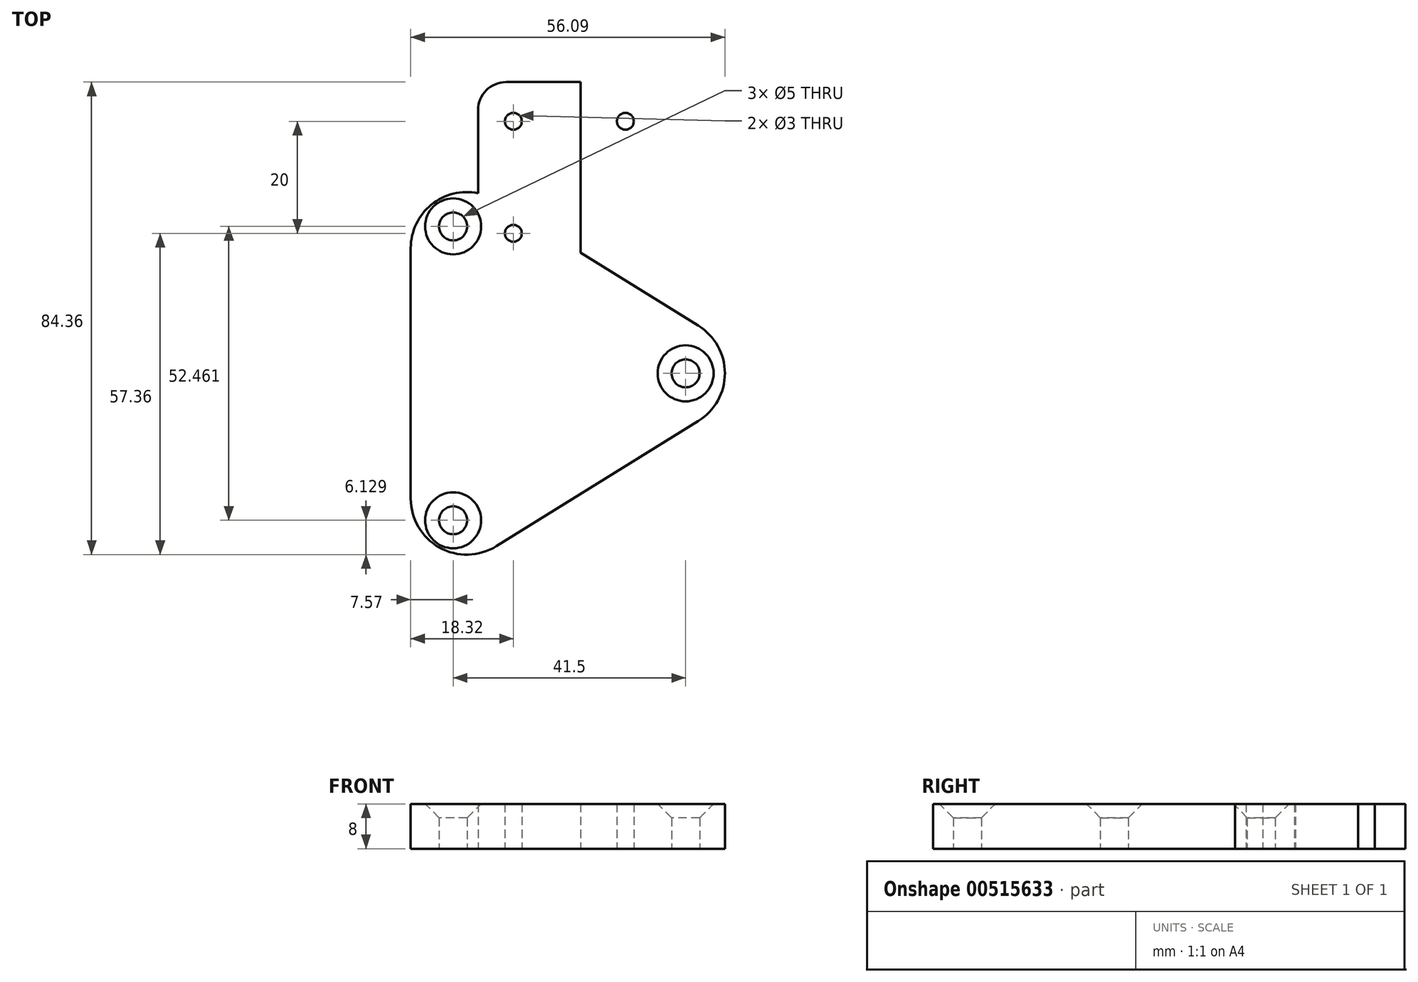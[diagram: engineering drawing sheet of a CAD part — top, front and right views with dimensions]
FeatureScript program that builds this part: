
annotation { "Feature Type Name" : "Feature", "Feature Type Description" : "" }
export const myFeature = defineFeature(function(context is Context, id is Id, definition is map)
    precondition{}
    {
        {
            var Q0;
            Q0=qCreatedBy(makeId("Top.planeOp"),FACE);
            var sketch = newSketch(context, id + "F0", { "sketchPlane" : qUnion([Q0])});
            skCircle(sketch, "E0", {"center": v(-22.75, 26.23) * mm, "radius": 2.5 * mm});
            skCircle(sketch, "E1.MirrorC", {"center": v(-22.75, -26.23) * mm, "radius": 2.5 * mm});
            skCircle(sketch, "E2", {"center": v(18.75, 0) * mm, "radius": 2.5 * mm});
            skCircle(sketch, "E3", {"center": v(-12, 45) * mm, "radius": 1.5 * mm});
            skCircle(sketch, "E4.MirrorC", {"center": v(8, 45) * mm, "radius": 1.5 * mm});
            skCircle(sketch, "E5.MirrorC", {"center": v(8, 25) * mm, "radius": 1.5 * mm});
            skLineSegment(sketch, "E6", {"start": v(21.03, -8.5) * mm, "end": v(-15.05, -30.86) * mm});
            skLineSegment(sketch, "E7", {"start": v(21.03, 8.5) * mm, "end": v(-15.05, 30.86) * mm});
            skPoint(sketch, "E8", {"position": v(34.75, 0) * mm});
            skLineSegment(sketch, "E9", {"start": v(-30.32, -22.36) * mm, "end": v(-30.32, 22.36) * mm});
            skPoint(sketch, "E10.visualSharp", {"position": v(-30.32, 40.33) * mm});
            skArc(sketch, "E10.filletArc", {"start": v(-15.05, 30.86) * mm, "mid": v(-25.18, 31.1) * mm, "end": v(-30.32, 22.36) * mm});
            skPoint(sketch, "E11.visualSharp", {"position": v(-30.32, -40.33) * mm});
            skArc(sketch, "E11.filletArc", {"start": v(-30.32, -22.36) * mm, "mid": v(-25.18, -31.1) * mm, "end": v(-15.05, -30.86) * mm});
            skArc(sketch, "E12.filletArc", {"start": v(21.03, -8.5) * mm, "mid": v(25.77, 0) * mm, "end": v(21.03, 8.5) * mm});
            skCircle(sketch, "E13", {"center": v(-12, 25) * mm, "radius": 1.5 * mm});
            skLineSegment(sketch, "E14.top", {"start": v(-13.3, 52) * mm, "end": v(9.3, 52) * mm});
            skLineSegment(sketch, "E14.left", {"start": v(-18.3, 32.16) * mm, "end": v(-18.3, 47) * mm});
            skLineSegment(sketch, "E14.right", {"start": v(14.3, 12.67) * mm, "end": v(14.3, 47) * mm});
            skPoint(sketch, "E15.visualSharp", {"position": v(-18.3, 52) * mm});
            skArc(sketch, "E15.filletArc", {"start": v(-13.3, 52) * mm, "mid": v(-16.84, 50.53) * mm, "end": v(-18.3, 47) * mm});
            skPoint(sketch, "E16.visualSharp", {"position": v(14.3, 52) * mm});
            skArc(sketch, "E16.filletArc", {"start": v(14.3, 47) * mm, "mid": v(12.84, 50.53) * mm, "end": v(9.3, 52) * mm});
            skLineSegment(sketch, "E17", {"start": v(-4, 52) * mm, "end": v(-4, -24.02) * mm});
            skLineSegment(sketch, "E18", {"start": v(0, 52) * mm, "end": v(0, -21.54) * mm});
            skSolve(sketch);
        }
        {
            var Q0;
            Q0=makeQuery(id+"F0.imprint","IMPRINT",FACE,{"disambiguationData":[TD([[makeQuery(id+"F0.imprint","IMPRINT",EDGE,{"derivedFrom":sQuery(id+"F0.wireOp",EDGE,"E0")}),-1.0]])]});
            var Q1;
            {var subQ0=sQuery(id+"F0.wireOp",EDGE,"E17");var subQ1=sQuery(id+"F0.wireOp",EDGE,"E6");var subQ2=makeQuery(id+"F0.imprint","INTERSECT",VERTEX,{"derivedFrom":[subQ1,subQ0]});Q1=makeQuery(id+"F0.imprint","IMPRINT",FACE,{"disambiguationData":[TD([[makeQuery(id+"F0.imprint","IMPRINT",EDGE,{"disambiguationData":[TD([[subQ2,1.0]])],"derivedFrom":subQ1}),-1.0]])]});}
            var Q2;
            Q2=makeQuery(id+"F0.imprint","IMPRINT",FACE,{"disambiguationData":[TD([[makeQuery(id+"F0.imprint","IMPRINT",EDGE,{"derivedFrom":sQuery(id+"F0.wireOp",EDGE,"E2")}),-1.0]])]});
            var Q3;
            Q3=makeQuery(id+"F0.imprint","IMPRINT",FACE,{"disambiguationData":[TD([[makeQuery(id+"F0.imprint","IMPRINT",EDGE,{"derivedFrom":sQuery(id+"F0.wireOp",EDGE,"E4.MirrorC")}),1.0]])]});
            var Q4;
            {var subQ0=sQuery(id+"F0.wireOp",EDGE,"E18");var subQ1=sQuery(id+"F0.wireOp",EDGE,"E7");var subQ2=makeQuery(id+"F0.imprint","INTERSECT",VERTEX,{"derivedFrom":[subQ1,subQ0]});Q4=makeQuery(id+"F0.imprint","IMPRINT",FACE,{"disambiguationData":[TD([[makeQuery(id+"F0.imprint","IMPRINT",EDGE,{"disambiguationData":[TD([[subQ2,-1.0]])],"derivedFrom":subQ1}),-1.0]])]});}
            var Q5;
            Q5=makeQuery(id+"F0.imprint","IMPRINT",FACE,{"disambiguationData":[TD([[makeQuery(id+"F0.imprint","IMPRINT",EDGE,{"derivedFrom":sQuery(id+"F0.wireOp",EDGE,"E3")}),-1.0]])]});
            extrude(context, id + "F1", {"entities" : qUnion([Q0, Q1, Q2, Q3, Q4, Q5]), "depth" : 8 * mm, "offsetDistance" : 25 * mm});
        }
        {
            var Q0;
            Q0=makeQuery(id+"F1.opExtrude","CAP_EDGE",EDGE,{"disambiguationData":[OSD([sQuery(id+"F0.wireOp",EDGE,"E1.MirrorC")])],"isStart":false});
            var Q1;
            Q1=makeQuery(id+"F1.opExtrude","CAP_EDGE",EDGE,{"disambiguationData":[OSD([sQuery(id+"F0.wireOp",EDGE,"E0")])],"isStart":false});
            var Q2;
            Q2=makeQuery(id+"F1.opExtrude","CAP_EDGE",EDGE,{"disambiguationData":[OSD([sQuery(id+"F0.wireOp",EDGE,"E2")])],"isStart":false});
            chamfer(context, id + "F2", {"entities" : qUnion([Q0, Q1, Q2]), "width" : 2.5 * mm, "tangentPropagation" : true});
        }
    });
